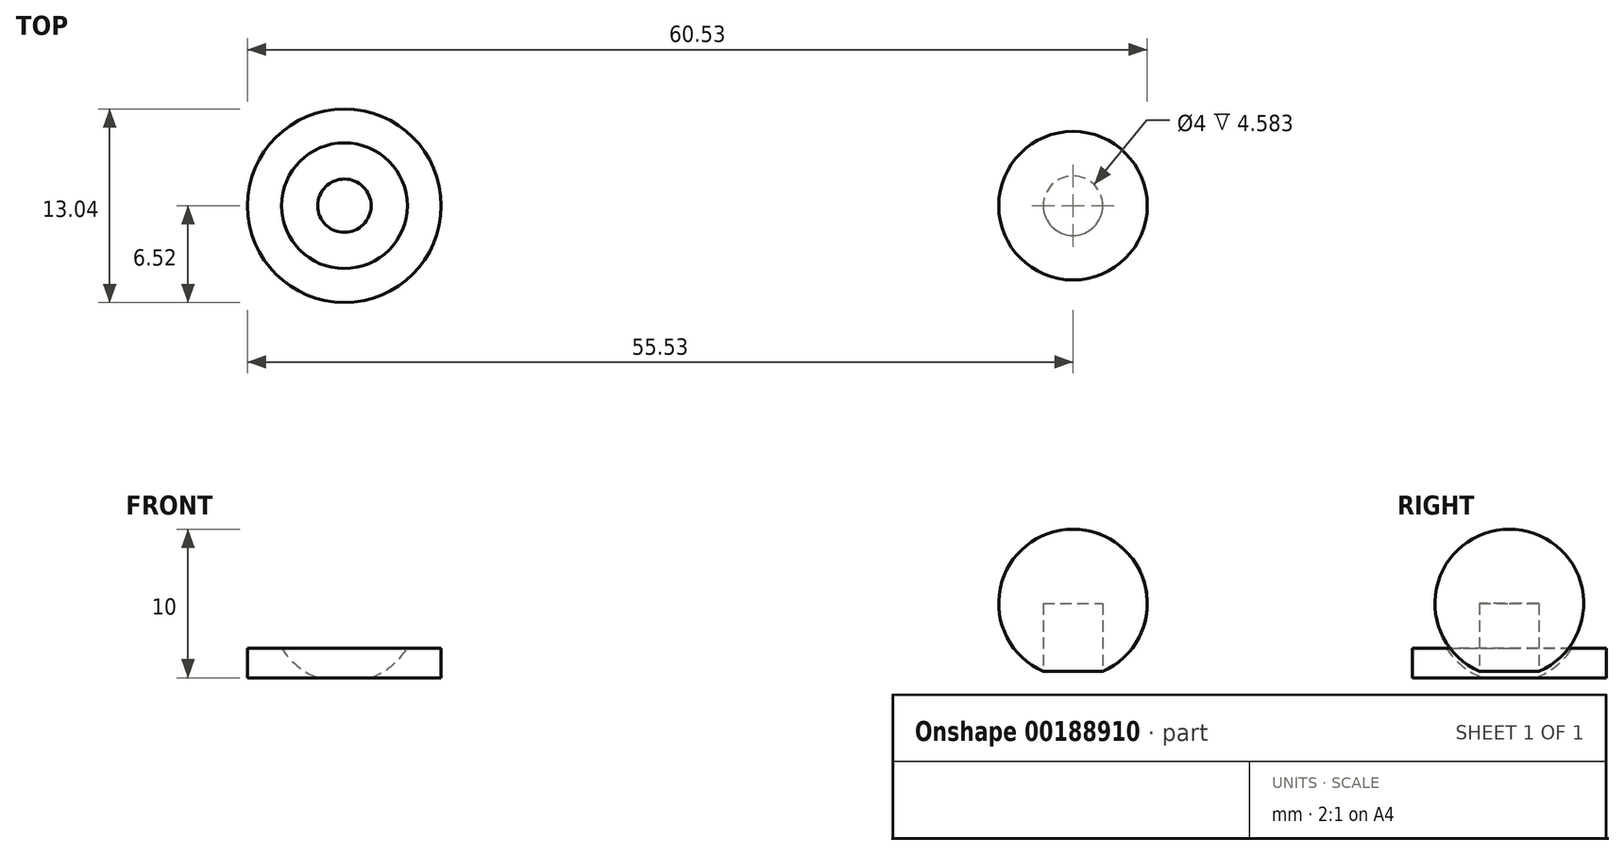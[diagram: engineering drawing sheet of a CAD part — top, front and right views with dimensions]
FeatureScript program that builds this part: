
annotation { "Feature Type Name" : "Feature", "Feature Type Description" : "" }
export const myFeature = defineFeature(function(context is Context, id is Id, definition is map)
    precondition{}
    {
        {
            var Q0;
            Q0=qCreatedBy(makeId("Front.planeOp"),FACE);
            var sketch = newSketch(context, id + "F0", { "sketchPlane" : qUnion([Q0])});
            skLineSegment(sketch, "E0", {"start": v(-2, 0.42) * mm, "end": v(-2, 5) * mm});
            skLineSegment(sketch, "E1", {"start": v(-2, 5) * mm, "end": v(0, 5) * mm});
            skLineSegment(sketch, "E2", {"start": v(0, 5) * mm, "end": v(0, 10) * mm});
            skArc(sketch, "E3", {"start": v(0, 10) * mm, "mid": v(-4.9, 6.02) * mm, "end": v(-2, 0.42) * mm});
            skPoint(sketch, "E4.orphan", {"position": v(-2, 0) * mm});
            skSolve(sketch);
        }
        {
            var Q0;
            Q0=qSketchRegion(id+"F0",true);
            var Q1;
            Q1=sQuery(id+"F0.wireOp",EDGE,"E2");
            revolve(context, id + "F1", {"entities" : qUnion([Q0]), "axis" : qUnion([Q1]), "revolveType" : RevolveType.FULL});
        }
        {
            var Q0;
            Q0=qCreatedBy(makeId("Front.planeOp"),FACE);
            var sketch = newSketch(context, id + "F2", { "sketchPlane" : qUnion([Q0])});
            skLineSegment(sketch, "E5", {"start": v(-50.8, 0) * mm, "end": v(-55.53, 0) * mm});
            skLineSegment(sketch, "E6", {"start": v(-55.53, 0) * mm, "end": v(-55.53, 2) * mm});
            skArc(sketch, "E7", {"start": v(-53.24, 2) * mm, "mid": v(-52.19, 0.8) * mm, "end": v(-50.8, 0) * mm});
            skLineSegment(sketch, "E8", {"start": v(-49.01, 4.67) * mm, "end": v(-49.01, 0) * mm, "construction": true});
            skLineSegment(sketch, "E9", {"start": v(-55.53, 2) * mm, "end": v(-53.24, 2) * mm});
            skSolve(sketch);
        }
        {
            var Q0;
            Q0=qSketchRegion(id+"F2",true);
            var Q1;
            Q1=sQuery(id+"F2.wireOp",EDGE,"E8");
            revolve(context, id + "F3", {"entities" : qUnion([Q0]), "axis" : qUnion([Q1]), "revolveType" : RevolveType.FULL});
        }
    });
